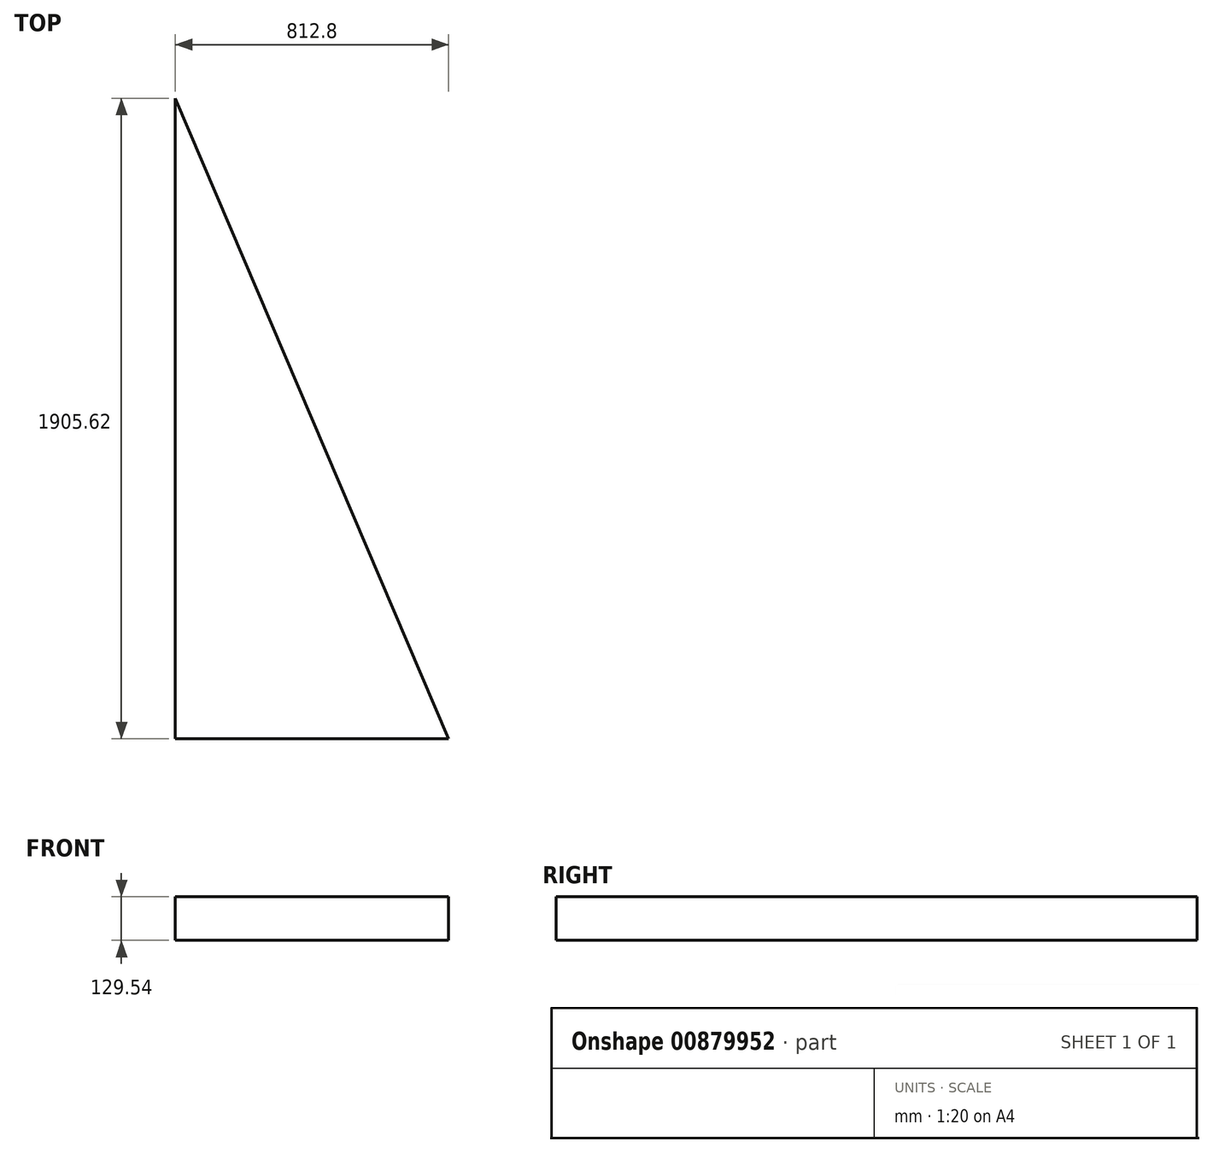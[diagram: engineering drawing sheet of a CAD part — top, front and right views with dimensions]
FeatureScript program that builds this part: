
annotation { "Feature Type Name" : "Feature", "Feature Type Description" : "" }
export const myFeature = defineFeature(function(context is Context, id is Id, definition is map)
    precondition{}
    {
        {
            var Q0;
            Q0=qCreatedBy(makeId("Top.planeOp"),FACE);
            var sketch = newSketch(context, id + "F0", { "sketchPlane" : qUnion([Q0])});
            skLineSegment(sketch, "E0", {"start": v(0, 1085.45) * mm, "end": v(812.8, -820.17) * mm});
            skLineSegment(sketch, "E1", {"start": v(812.8, -820.17) * mm, "end": v(0, -820.17) * mm});
            skLineSegment(sketch, "E2", {"start": v(0, 1085.45) * mm, "end": v(0, -820.17) * mm});
            skSolve(sketch);
        }
        {
            var Q0;
            Q0 = qSketchRegion(id + "F0", true);
            extrude(context, id + "F1", {"entities" : qUnion([Q0]), "depth" : 129.54 * mm, "offsetDistance" : 25.4 * mm});
        }
    });
